# Revit family: QPTS
name_source: partatom
category: Mechanical Equipment
revit_build: Autodesk Revit 2018 (Build: 20170223_1515(x64)
units: mm (PartAtom-declared; Revit-internal decimal feet)

## family parameters
Always vertical = Yes
Cut with Voids When Loaded = No
Part Type = Normal
Room Calculation Point = No
Round Connector Dimension = Use Radius
Shared = No
Work Plane-Based = No

## types (52) — shared parameters
Description = Series Fan Powered Air Terminal with Hot Water Coil
Discharge = 1/2"
Enclosure Depth = 6 1/2"
Filter = 1"
Manufacturer = Anemostat
Model = QPTW
URL = http://www.anemostat.com

## per-type parameters (varying)
| type | Diameter | Discharge "Z" | Discharge Height "Y" | Discharge Width "X" | Duct Inlet Radius | Height | Induction | Induction Height "D" | Induction Width "C" | Length | Q5 Sound Elbow | Q5B | Q5Q | Radius | Width |
| 11706 QPTS 1/6-hp - 06" W/Out S/Elbow | 5 7/8" | 3" | 11" | 11 1/2" | 3" | 15" | Yes | 12" | 13" | 30" | No | 18" | 18" | 2 15/16" | 34" |
| 25009 QPTS 1/2-hp - 09" W/Out S/Elbow | 8 7/8" | 3" | 12" | 14" | 4" | 18" | Yes | 16" | 17" | 34" | No | 20" | 18" | 4 7/16" | 40" |
| 25009 QPTS 1/2-hp - 09" with S/Elbow | 8 7/8" | 3" | 12" | 14" | 4" | 18" | No | 16" | 17" | 34" | Yes | 20" | 18" | 4 7/16" | 40" |
| 25010 QPTS 1/2-hp - 10" W/Out S/Elbow | 9 7/8" | 3" | 12" | 14" | 5" | 18" | Yes | 16" | 17" | 34" | No | 20" | 18" | 4 15/16" | 40" |
| 25010 QPTS 1/2-hp - 10" with S/Elbow | 9 7/8" | 3" | 12" | 14" | 5" | 18" | No | 16" | 17" | 34" | Yes | 20" | 18" | 4 15/16" | 40" |
| 25012 QPTS 1/2-hp - 12" W/Out S/Elbow | 11 7/8" | 3" | 12" | 14" | 6" | 18" | Yes | 16" | 17" | 34" | No | 20" | 18" | 5 15/16" | 40" |
| 25012 QPTS 1/2-hp - 12" with S/Elbow | 11 7/8" | 3" | 12" | 14" | 6" | 18" | No | 16" | 17" | 34" | Yes | 20" | 18" | 5 15/16" | 40" |
| 31012 QPTS 1-hp - 12" with S/Elbow | 11 7/8" | 2 1/4" | 16" | 19" | 6" | 20" | No | 18" | 21" | 40" | Yes | 23" | 20" | 5 15/16" | 46" |
| 31012 QPTS 1-hp - 12" W/Out S/Elbow | 11 7/8" | 2 1/4" | 16" | 19" | 6" | 20" | Yes | 18" | 21" | 40" | No | 23" | 20" | 5 15/16" | 46" |
| 31014 QPTS 1-hp - 14" W/Out S/Elbow | 13 7/8" | 2 1/4" | 16" | 19" | 7" | 20" | Yes | 18" | 21" | 40" | No | 23" | 20" | 6 15/16" | 46" |
| 31014 QPTS 1-hp - 14" with S/Elbow | 13 7/8" | 2 1/4" | 16" | 19" | 7" | 20" | No | 18" | 21" | 40" | Yes | 23" | 20" | 6 15/16" | 46" |
| 31016 QPTS 1-hp - 16" W/Out S/Elbow | 15 7/8" | 2 1/4" | 16" | 19" | 8" | 20" | Yes | 18" | 21" | 40" | No | 23" | 20" | 7 15/16" | 46" |
| 31016 QPTS 1-hp - 16" with S/Elbow | 15 7/8" | 2 1/4" | 16" | 19" | 8" | 20" | No | 18" | 21" | 40" | Yes | 23" | 20" | 7 15/16" | 46" |
| 37516 QPTS 3/4-hp - 16" W/Out S/Elbow | 15 7/8" | 2 1/4" | 16" | 19" | 8" | 20" | Yes | 18" | 21" | 40" | No | 23" | 20" | 7 15/16" | 46" |
| 37514 QPTS 3/4-hp - 14" W/Out S/Elbow | 13 7/8" | 2 1/4" | 16" | 19" | 7" | 20" | Yes | 18" | 21" | 40" | No | 23" | 20" | 6 15/16" | 46" |
| 37512 QPTS 3/4-hp - 12" W/Out S/Elbow | 11 7/8" | 2 1/4" | 16" | 19" | 6" | 20" | Yes | 18" | 21" | 40" | No | 23" | 20" | 5 15/16" | 46" |
| 35012 QPTS 1/2-hp - 12" W/Out S/Elbow | 11 7/8" | 2 1/4" | 16" | 19" | 6" | 20" | Yes | 18" | 21" | 40" | No | 23" | 20" | 5 15/16" | 46" |
| 35012 QPTS 1/2-hp - 12" with S/Elbow | 11 7/8" | 2 1/4" | 16" | 19" | 6" | 20" | No | 18" | 21" | 40" | Yes | 23" | 20" | 5 15/16" | 46" |
| 35014 QPTS 1/2-hp - 14" with S/Elbow | 13 7/8" | 2 1/4" | 16" | 19" | 7" | 20" | No | 18" | 21" | 40" | Yes | 23" | 20" | 6 15/16" | 46" |
| 35014 QPTS 1/2-hp - 14" W/Out S/Elbow | 13 7/8" | 2 1/4" | 16" | 19" | 7" | 20" | Yes | 18" | 21" | 40" | No | 23" | 20" | 6 15/16" | 46" |
| 35016 QPTS 1/2-hp - 16" W/Out S/Elbow | 15 7/8" | 2 1/4" | 16" | 19" | 8" | 20" | Yes | 18" | 21" | 40" | No | 23" | 20" | 7 15/16" | 46" |
| 35016 QPTS 1/2-hp - 16" with S/Elbow | 15 7/8" | 2 1/4" | 16" | 19" | 8" | 20" | No | 18" | 21" | 40" | Yes | 23" | 20" | 7 15/16" | 46" |
| 37512 QPTS 3/4-hp - 12" with S/Elbow | 11 7/8" | 2 1/4" | 16" | 19" | 6" | 20" | No | 18" | 21" | 40" | Yes | 23" | 20" | 5 15/16" | 46" |
| 37514 QPTS 3/4-hp - 14" with S/Elbow | 13 7/8" | 2 1/4" | 16" | 19" | 7" | 20" | No | 18" | 21" | 40" | Yes | 23" | 20" | 6 15/16" | 46" |
| 37516 QPTS 3/4-hp - 16" with S/Elbow | 15 7/8" | 2 1/4" | 16" | 19" | 8" | 20" | No | 18" | 21" | 40" | Yes | 23" | 20" | 7 15/16" | 46" |
| 22509 QPTS 1/4-hp - 09" W/Out S/Elbow | 8 7/8" | 3" | 12" | 14" | 4" | 18" | Yes | 16" | 17" | 34" | No | 20" | 18" | 4 7/16" | 40" |
| 22510 QPTS 1/4-hp - 10" W/Out S/Elbow | 9 7/8" | 3" | 12" | 14" | 5" | 18" | Yes | 16" | 17" | 34" | No | 20" | 18" | 4 15/16" | 40" |
| 22512 QPTS 1/4-hp - 12" W/Out S/Elbow | 11 7/8" | 3" | 12" | 14" | 6" | 18" | Yes | 16" | 17" | 34" | No | 20" | 18" | 5 15/16" | 40" |
| 22512 QPTS 1/4-hp - 12" with S/Elbow | 11 7/8" | 3" | 12" | 14" | 6" | 18" | No | 16" | 17" | 34" | Yes | 20" | 18" | 5 15/16" | 40" |
| 22509 QPTS 1/4-hp - 09" with S/Elbow | 8 7/8" | 3" | 12" | 14" | 4" | 18" | No | 16" | 17" | 34" | Yes | 20" | 18" | 4 7/16" | 40" |
| 22510 QPTS 1/4-hp - 10" with S/Elbow | 9 7/8" | 3" | 12" | 14" | 5" | 18" | No | 16" | 17" | 34" | Yes | 20" | 18" | 4 15/16" | 40" |
| 21709 QPTS 1/6-hp - 09" W/Out S/Elbow | 8 7/8" | 3" | 12" | 14" | 4" | 18" | Yes | 16" | 17" | 34" | No | 20" | 18" | 4 7/16" | 40" |
| 21709 QPTS 1/6-hp - 09" with S/Elbow | 8 7/8" | 3" | 12" | 14" | 4" | 18" | No | 16" | 17" | 34" | Yes | 20" | 18" | 4 7/16" | 40" |
| 21710 QPTS 1/6-hp - 10" W/Out S/Elbow | 9 7/8" | 3" | 12" | 14" | 5" | 18" | Yes | 16" | 17" | 34" | No | 20" | 18" | 4 15/16" | 40" |
| 21710 QPTS 1/6-hp - 10" with S/Elbow | 9 7/8" | 3" | 12" | 14" | 5" | 18" | No | 16" | 17" | 34" | Yes | 20" | 18" | 4 15/16" | 40" |
| 21712 QPTS 1/6-hp - 12" W/Out S/Elbow | 11 7/8" | 3" | 12" | 14" | 6" | 18" | Yes | 16" | 17" | 34" | No | 20" | 18" | 5 15/16" | 40" |
| 21712 QPTS 1/6-hp - 12" with S/Elbow | 11 7/8" | 3" | 12" | 14" | 6" | 18" | No | 16" | 17" | 34" | Yes | 20" | 18" | 5 15/16" | 40" |
| 11706 QPTS 1/6-hp - 06" with S/Elbow | 5 7/8" | 3" | 11" | 11 1/2" | 3" | 15" | No | 12" | 13" | 30" | Yes | 18" | 18" | 2 15/16" | 34" |
| 11707 QPTS 1/6-hp - 07" W/Out S/Elbow | 6 7/8" | 3" | 11" | 11 1/2" | 3" | 15" | Yes | 12" | 13" | 30" | No | 18" | 18" | 3 7/16" | 34" |
| 11708 QPTS 1/6-hp - 08" W/Out S/Elbow | 7 7/8" | 3" | 11" | 11 1/2" | 4" | 15" | Yes | 12" | 13" | 30" | No | 18" | 18" | 3 15/16" | 34" |
| 11709 QPTS 1/6-hp - 09" W/Out S/Elbow | 8 7/8" | 3" | 11" | 11 1/2" | 4" | 15" | Yes | 12" | 13" | 30" | No | 18" | 18" | 4 7/16" | 34" |
| 11709 QPTS 1/6-hp - 09" with S/Elbow | 8 7/8" | 3" | 11" | 11 1/2" | 4" | 15" | No | 12" | 13" | 30" | Yes | 18" | 18" | 4 7/16" | 34" |
| 11708 QPTS 1/6-hp - 08" with S/Elbow | 7 7/8" | 3" | 11" | 11 1/2" | 4" | 15" | No | 12" | 13" | 30" | Yes | 18" | 18" | 3 15/16" | 34" |
| 11707 QPTS 1/6-hp - 07" with S/Elbow | 6 7/8" | 3" | 11" | 11 1/2" | 3" | 15" | No | 12" | 13" | 30" | Yes | 18" | 18" | 3 7/16" | 34" |
| 12506 QPTS 1/4-hp - 06" W/Out S/Elbow | 5 7/8" | 3" | 11" | 11 1/2" | 3" | 15" | Yes | 12" | 13" | 30" | No | 18" | 18" | 2 15/16" | 34" |
| 12507 QPTS 1/4-hp - 07" W/Out S/Elbow | 6 7/8" | 3" | 11" | 11 1/2" | 3" | 15" | Yes | 12" | 13" | 30" | No | 18" | 18" | 3 7/16" | 34" |
| 12508 QPTS 1/4-hp - 08" W/Out S/Elbow | 7 7/8" | 3" | 11" | 11 1/2" | 4" | 15" | Yes | 12" | 13" | 30" | No | 18" | 18" | 3 15/16" | 34" |
| 12509 QPTS 1/4-hp - 09" W/Out S/Elbow | 8 7/8" | 3" | 11" | 11 1/2" | 4" | 15" | Yes | 12" | 13" | 30" | No | 18" | 18" | 4 7/16" | 34" |
| 12506 QPTS 1/4-hp - 06" with S/Elbow | 5 7/8" | 3" | 11" | 11 1/2" | 3" | 15" | No | 12" | 13" | 30" | Yes | 18" | 18" | 2 15/16" | 34" |
| 12507 QPTS 1/4-hp - 07" with S/Elbow | 6 7/8" | 3" | 11" | 11 1/2" | 3" | 15" | No | 12" | 13" | 30" | Yes | 18" | 18" | 3 7/16" | 34" |
| 12508 QPTS 1/4-hp - 08" with S/Elbow | 7 7/8" | 3" | 11" | 11 1/2" | 4" | 15" | Yes | 12" | 13" | 30" | No | 18" | 18" | 3 15/16" | 34" |
| 12509 QPTS 1/4-hp - 09" with S/Elbow | 8 7/8" | 3" | 11" | 11 1/2" | 4" | 15" | Yes | 12" | 13" | 30" | No | 18" | 18" | 4 7/16" | 34" |

## geometry (parser evidence)
native form markers: Sweep x3
no freeform markers — native parametric forms only
